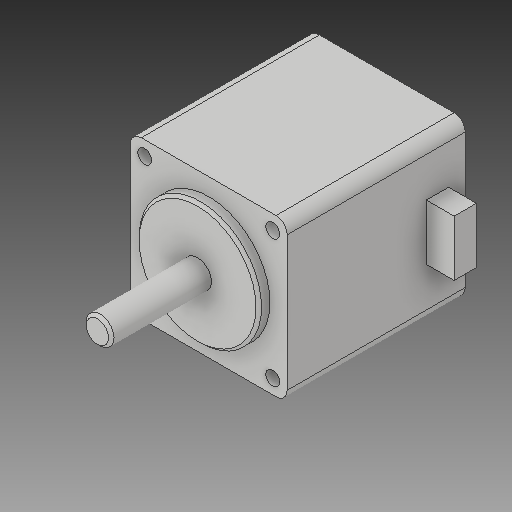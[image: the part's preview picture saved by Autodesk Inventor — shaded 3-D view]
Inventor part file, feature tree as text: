
AUTODESK INVENTOR PART (.ipt)
format: ipt  version: 2019 (Build 230136000, 136)  size: 177,664 bytes
history: native  units: mm
features: extrude x5, sketch x5, chamfer x2, fillet x1
ambient origin geometry x8: Origin, YZ Plane, XZ Plane, XY Plane, X Axis, Y Axis, Z Axis, Center Point
bodies: Solid1 (feature_tree)
feature tree (13):
  extrude  "Extrusion1"  Depth=28.2mm
  extrude  "Extrusion2"  Depth=32.0mm
  extrude  "Extrusion3"  Depth=2.5mm
  extrude  "Extrusion4"  Depth=4.5mm TaperAngle=0.0deg
  fillet  "Fillet1"  Radius=22.0mm
  chamfer  "Chamfer1"  Distance=2.0mm
  chamfer  "Chamfer2"  Distance=18.0mm
  extrude  "Extrusion5"  Depth=2.0mm
  sketch  "Sketch1"  dims[d0=28.2mm d1=28.2mm]
  sketch  "Sketch2"  dims[d2=32.0mm d3=0.0mm d4=23.0mm]
  sketch  "Sketch3"  dims[d5=23.0mm d6=2.5mm]
  sketch  "Sketch4"  dims[d7=40.0mm d9=360.0deg d11=4.5mm d12=0.0mm d13=22.0mm d14=2.0mm d15=0.0mm]
  sketch  "Sketch5"  dims[d16=5.0mm d17=18.0mm d18=0.0mm d19=2.0mm d20=0.5mm d21=2.0mm d22=45.0deg d23=0.5mm d24=2.0mm d25=45.0deg d26=5.0mm d27=4.0mm d28=10.0mm d29=5.0mm d30=0.0mm]
